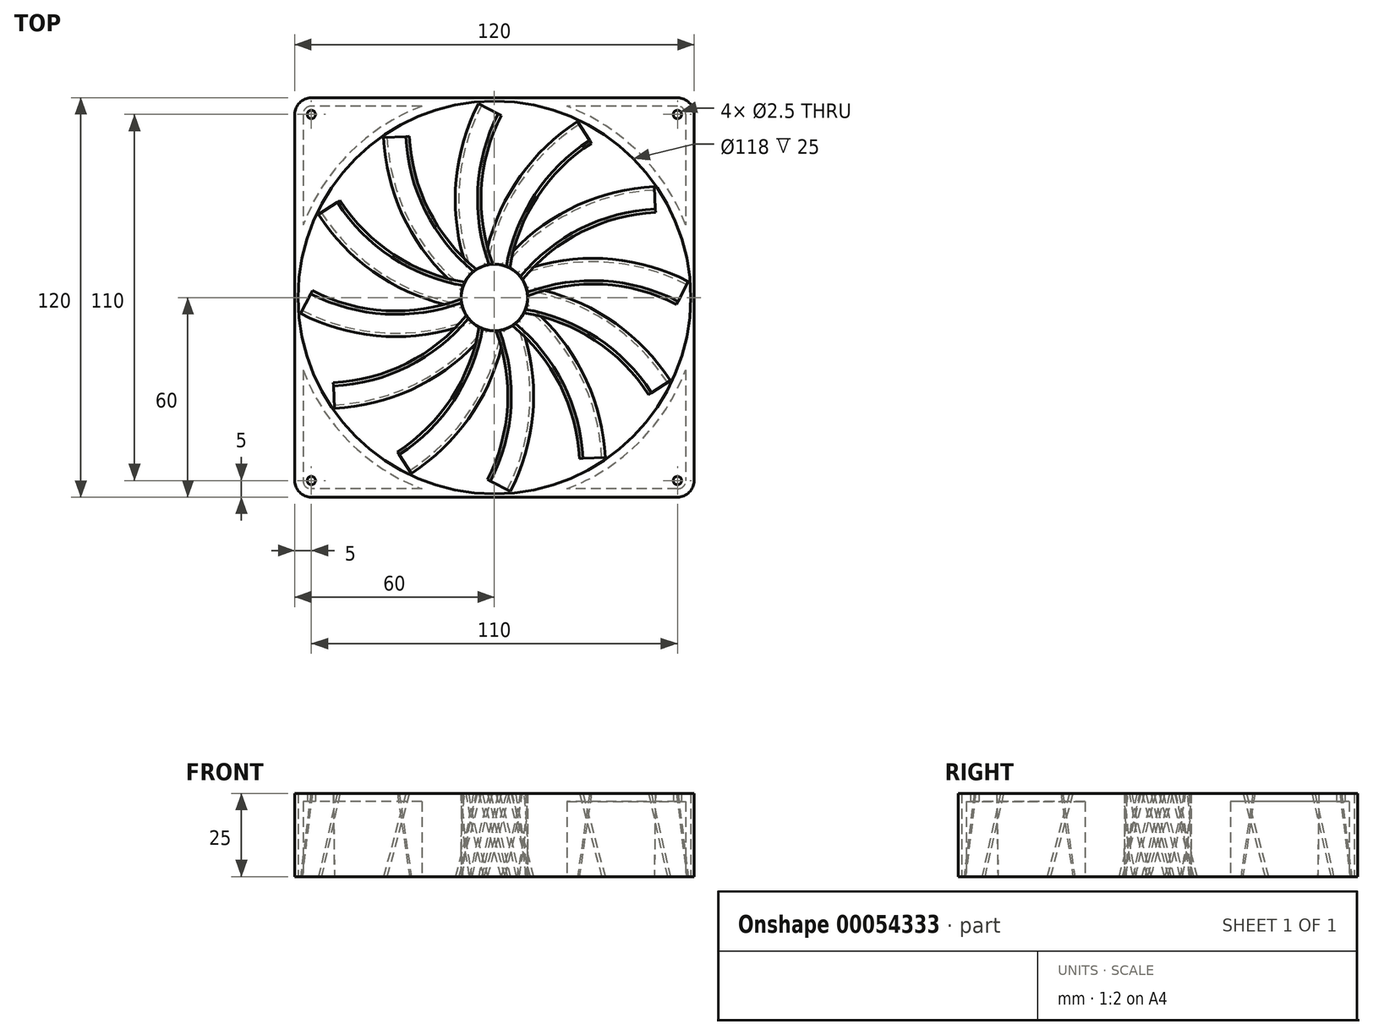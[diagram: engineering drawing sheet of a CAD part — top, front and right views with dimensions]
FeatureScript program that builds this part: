
annotation { "Feature Type Name" : "Feature", "Feature Type Description" : "" }
export const myFeature = defineFeature(function(context is Context, id is Id, definition is map)
    precondition{}
    {
        {
            var Q0;
            Q0=qCreatedBy(makeId("Top.planeOp"),FACE);
            var sketch = newSketch(context, id + "F0", { "sketchPlane" : qUnion([Q0])});
            skCircle(sketch, "E0", {"center": v(0, 0) * mm, "radius": 59 * mm});
            skCircle(sketch, "E1", {"center": v(0, 0) * mm, "radius": 10 * mm});
            skLineSegment(sketch, "E2", {"start": v(0, 0) * mm, "end": v(0, 59) * mm, "construction": true});
            skArc(sketch, "E3", {"start": v(27.05, 49.6) * mm, "mid": v(7.2, 28.25) * mm, "end": v(0, 0) * mm});
            skLineSegment(sketch, "E4.rect.bottom", {"start": v(60, 60) * mm, "end": v(-60, 60) * mm});
            skLineSegment(sketch, "E4.rect.top", {"start": v(60, -60) * mm, "end": v(-60, -60) * mm});
            skLineSegment(sketch, "E4.rect.left", {"start": v(60, 60) * mm, "end": v(60, -60) * mm});
            skLineSegment(sketch, "E4.rect.right", {"start": v(-60, 60) * mm, "end": v(-60, -60) * mm});
            skCircle(sketch, "E5", {"center": v(0, 0) * mm, "radius": 56.5 * mm, "construction": true});
            skPoint(sketch, "E6", {"position": v(-55, -55) * mm});
            skPoint(sketch, "E7", {"position": v(55, -55) * mm});
            skPoint(sketch, "E8", {"position": v(55, 55) * mm});
            skPoint(sketch, "E9", {"position": v(-55, 55) * mm});
            skSolve(sketch);
        }
        {
            var Q0;
            Q0=makeQuery(id+"F0.imprint","IMPRINT",FACE,{"disambiguationData":[TD([[makeQuery(id+"F0.imprint","IMPRINT",EDGE,{"derivedFrom":sQuery(id+"F0.wireOp",EDGE,"E1")}),1.0]])]});
            var Q1;
            Q1=sQuery(id+"F0.wireOp",EDGE,"E1");
            extrude(context, id + "F1", {"entities" : qUnion([Q0]), "surfaceEntities" : qUnion([Q1]), "depth" : (25 / 2) * mm, "hasSecondDirection" : true, "secondDirectionOppositeDirection" : true, "secondDirectionDepth" : (25 / 2) * mm});
        }
        {
            var Q0;
            Q0=makeQuery(id+"F0.imprint","IMPRINT",FACE,{"disambiguationData":[TD([[makeQuery(id+"F0.imprint","IMPRINT",EDGE,{"derivedFrom":sQuery(id+"F0.wireOp",EDGE,"E0")}),-1.0]])]});
            extrude(context, id + "F2", {"entities" : qUnion([Q0]), "depth" : (25 / 2) * mm, "hasSecondDirection" : true, "secondDirectionOppositeDirection" : true, "secondDirectionDepth" : (25 / 2) * mm});
        }
        {
            var Q0;
            Q0=makeQuery(id+"F2.opExtrude","SWEPT_EDGE",EDGE,{"disambiguationData":[OSD([sQuery(id+"F0.wireOp",EDGE,"E4.rect.top"),sQuery(id+"F0.wireOp",EDGE,"E4.rect.left")])]});
            var Q1;
            Q1=makeQuery(id+"F2.opExtrude","SWEPT_EDGE",EDGE,{"disambiguationData":[OSD([sQuery(id+"F0.wireOp",EDGE,"E4.rect.top"),sQuery(id+"F0.wireOp",EDGE,"E4.rect.right")])]});
            var Q2;
            Q2=makeQuery(id+"F2.opExtrude","SWEPT_EDGE",EDGE,{"disambiguationData":[OSD([sQuery(id+"F0.wireOp",EDGE,"E4.rect.bottom"),sQuery(id+"F0.wireOp",EDGE,"E4.rect.right")])]});
            var Q3;
            Q3=makeQuery(id+"F2.opExtrude","SWEPT_EDGE",EDGE,{"disambiguationData":[OSD([sQuery(id+"F0.wireOp",EDGE,"E4.rect.bottom"),sQuery(id+"F0.wireOp",EDGE,"E4.rect.left")])]});
            fillet(context, id + "F3", {"entities" : qUnion([Q0, Q1, Q2, Q3]), "radius" : 5 * mm, "tangentPropagation" : true, "allowEdgeOverflow" : false});
        }
        {
            var Q0;
            Q0=makeQuery(id+"F2.opExtrude","CAP_FACE",FACE,{"disambiguationData":[OSD([sQuery(id+"F0.wireOp",EDGE,"E0"),sQuery(id+"F0.wireOp",EDGE,"E4.rect.bottom"),sQuery(id+"F0.wireOp",EDGE,"E4.rect.top"),sQuery(id+"F0.wireOp",EDGE,"E4.rect.left"),sQuery(id+"F0.wireOp",EDGE,"E4.rect.right")])],"isStart":true});
            shell(context, id + "F4", {"entities" : qUnion([Q0]), "thickness" : 2.5 * mm});
        }
        {
            var Q0;
            Q0=sQuery(id+"F0.wireOp",VERTEX,"E6");
            var Q1;
            Q1=sQuery(id+"F0.wireOp",VERTEX,"E7");
            var Q2;
            Q2=sQuery(id+"F0.wireOp",VERTEX,"E8");
            var Q3;
            Q3=sQuery(id+"F0.wireOp",VERTEX,"E9");
            var Q4;
            Q4=makeQuery(id+"F2.opExtrude","SWEPT_BODY",BODY,{"disambiguationData":[OSD([sQuery(id+"F0.wireOp",EDGE,"E0"),sQuery(id+"F0.wireOp",EDGE,"E4.rect.bottom"),sQuery(id+"F0.wireOp",EDGE,"E4.rect.top"),sQuery(id+"F0.wireOp",EDGE,"E4.rect.left"),sQuery(id+"F0.wireOp",EDGE,"E4.rect.right")])]});
            hole(context, id + "F5", {"style" : HoleStyle.SIMPLE, "holeDiameter" : 2.5 * mm, "endStyle" : HoleEndStyle.THROUGH, "oppositeDirection" : true, "locations" : qUnion([Q0, Q1, Q2, Q3]), "scope" : qUnion([Q4])});
        }
        {
            var Q0;
            Q0=qCreatedBy(makeId("Front.planeOp"),FACE);
            var sketch = newSketch(context, id + "F6", { "sketchPlane" : qUnion([Q0])});
            skLineSegment(sketch, "E10", {"start": v(3.35, 12.5) * mm, "end": v(-3.35, -12.5) * mm, "construction": true});
            skLineSegment(sketch, "E11.0", {"start": v(2.83, 12.5) * mm, "end": v(-3.87, -12.5) * mm});
            skLineSegment(sketch, "E12.0", {"start": v(3.87, 12.5) * mm, "end": v(-2.83, -12.5) * mm});
            skLineSegment(sketch, "E13", {"start": v(-2.83, -12.5) * mm, "end": v(-3.87, -12.5) * mm});
            skLineSegment(sketch, "E14", {"start": v(3.87, 12.5) * mm, "end": v(2.83, 12.5) * mm});
            skSolve(sketch);
        }
        {
            var Q0;
            Q0=makeQuery(id+"F6.imprint","IMPRINT",FACE,{"disambiguationData":[TD([[makeQuery(id+"F6.imprint","IMPRINT",EDGE,{"derivedFrom":sQuery(id+"F6.wireOp",EDGE,"E11.0")}),1.0]])]});
            var Q1;
            Q1=sQuery(id+"F0.wireOp",EDGE,"E3");
            sweep(context, id + "F7", {"operationType" : NewBodyOperationType.ADD, "profiles" : qUnion([Q0]), "path" : qUnion([Q1])});
        }
        {
            var Q0;
            Q0=makeQuery(id+"F1.opExtrude","SWEPT_BODY",BODY,{"disambiguationData":[OSD([sQuery(id+"F0.wireOp",EDGE,"E1")])]});
            var Q1;
            Q1=makeQuery(id+"F2.opExtrude","CAP_EDGE",EDGE,{"disambiguationData":[OSD([sQuery(id+"F0.wireOp",EDGE,"E0")])],"isStart":true});
            circularPattern(context, id + "F8", {"operationType" : NewBodyOperationType.ADD, "entities" : qUnion([Q0]), "axis" : qUnion([Q1]), "angle" : 30 * degree, "instanceCount" : 12});
        }
    });
